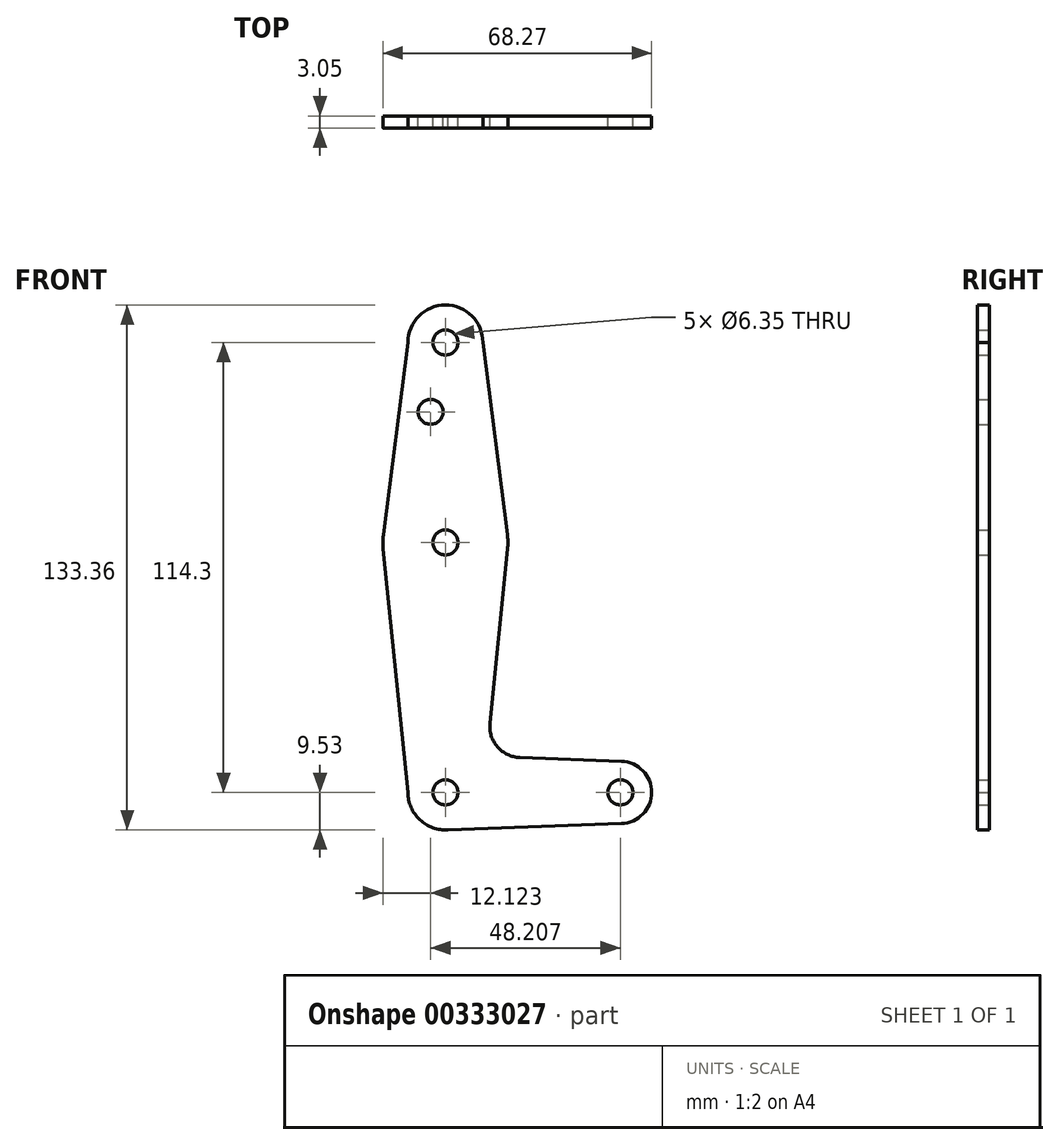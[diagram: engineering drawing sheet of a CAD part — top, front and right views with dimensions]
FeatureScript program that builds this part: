
annotation { "Feature Type Name" : "Feature", "Feature Type Description" : "" }
export const myFeature = defineFeature(function(context is Context, id is Id, definition is map)
    precondition{}
    {
        {
            var Q0;
            Q0=qCreatedBy(makeId("Front.planeOp"),FACE);
            var sketch = newSketch(context, id + "F0", { "sketchPlane" : qUnion([Q0])});
            skLineSegment(sketch, "E0", {"start": v(0, 114.3) * mm, "end": v(0, 0) * mm});
            skLineSegment(sketch, "E1", {"start": v(0, 0) * mm, "end": v(44.45, 0) * mm});
            skCircle(sketch, "E2", {"center": v(0, 114.3) * mm, "radius": 9.53 * mm});
            skCircle(sketch, "E3", {"center": v(0, 0) * mm, "radius": 9.53 * mm});
            skCircle(sketch, "E4", {"center": v(44.45, 0) * mm, "radius": 7.94 * mm});
            skCircle(sketch, "E5", {"center": v(0, 63.5) * mm, "radius": 15.88 * mm});
            skLineSegment(sketch, "E6", {"start": v(0, 114.3) * mm, "end": v(0, 63.5) * mm});
            skLineSegment(sketch, "E7", {"start": v(0, 63.5) * mm, "end": v(0, 0) * mm});
            skLineSegment(sketch, "E8", {"start": v(18.93, 8.85) * mm, "end": v(44.73, 7.93) * mm});
            skLineSegment(sketch, "E9", {"start": v(0, -9.53) * mm, "end": v(44.73, -7.93) * mm});
            skLineSegment(sketch, "E10", {"start": v(-9.52, 114.3) * mm, "end": v(-15.75, 65.5) * mm});
            skLineSegment(sketch, "E11", {"start": v(9.53, 114.3) * mm, "end": v(15.75, 65.5) * mm});
            skLineSegment(sketch, "E12", {"start": v(-9.53, 0) * mm, "end": v(-15.8, 61.9) * mm});
            skLineSegment(sketch, "E13", {"start": v(11.3, 17.6) * mm, "end": v(15.8, 61.9) * mm});
            skArc(sketch, "E14.filletArc", {"start": v(11.3, 17.6) * mm, "mid": v(13.22, 11.57) * mm, "end": v(18.93, 8.85) * mm});
            skCircle(sketch, "E15", {"center": v(0, 114.3) * mm, "radius": 3.18 * mm});
            skCircle(sketch, "E16", {"center": v(0, 63.5) * mm, "radius": 3.18 * mm});
            skCircle(sketch, "E17", {"center": v(0, 0) * mm, "radius": 3.18 * mm});
            skCircle(sketch, "E18", {"center": v(44.45, 0) * mm, "radius": 3.18 * mm});
            skCircle(sketch, "E19", {"center": v(-3.76, 96.7) * mm, "radius": 3.18 * mm});
            skSolve(sketch);
        }
        {
            var Q0;
            Q0 = qSketchRegion(id + "F0", true);
            var Q1;
            {var subQ0=sQuery(id+"F0.wireOp",EDGE,"E17");var subQ1=sQuery(id+"F0.wireOp",EDGE,"E1");var subQ2=makeQuery(id+"F0.imprint","INTERSECT",VERTEX,{"derivedFrom":[subQ1,subQ0]});Q1=makeQuery(id+"F0.imprint","IMPRINT",FACE,{"disambiguationData":[TD([[makeQuery(id+"F0.imprint","IMPRINT",EDGE,{"disambiguationData":[TD([[subQ2,-1.0]])],"derivedFrom":subQ1}),1.0]])]});}
            extrude(context, id + "F1", {"entities" : qUnion([Q0, Q1]), "depth" : 3.05 * mm});
        }
    });
